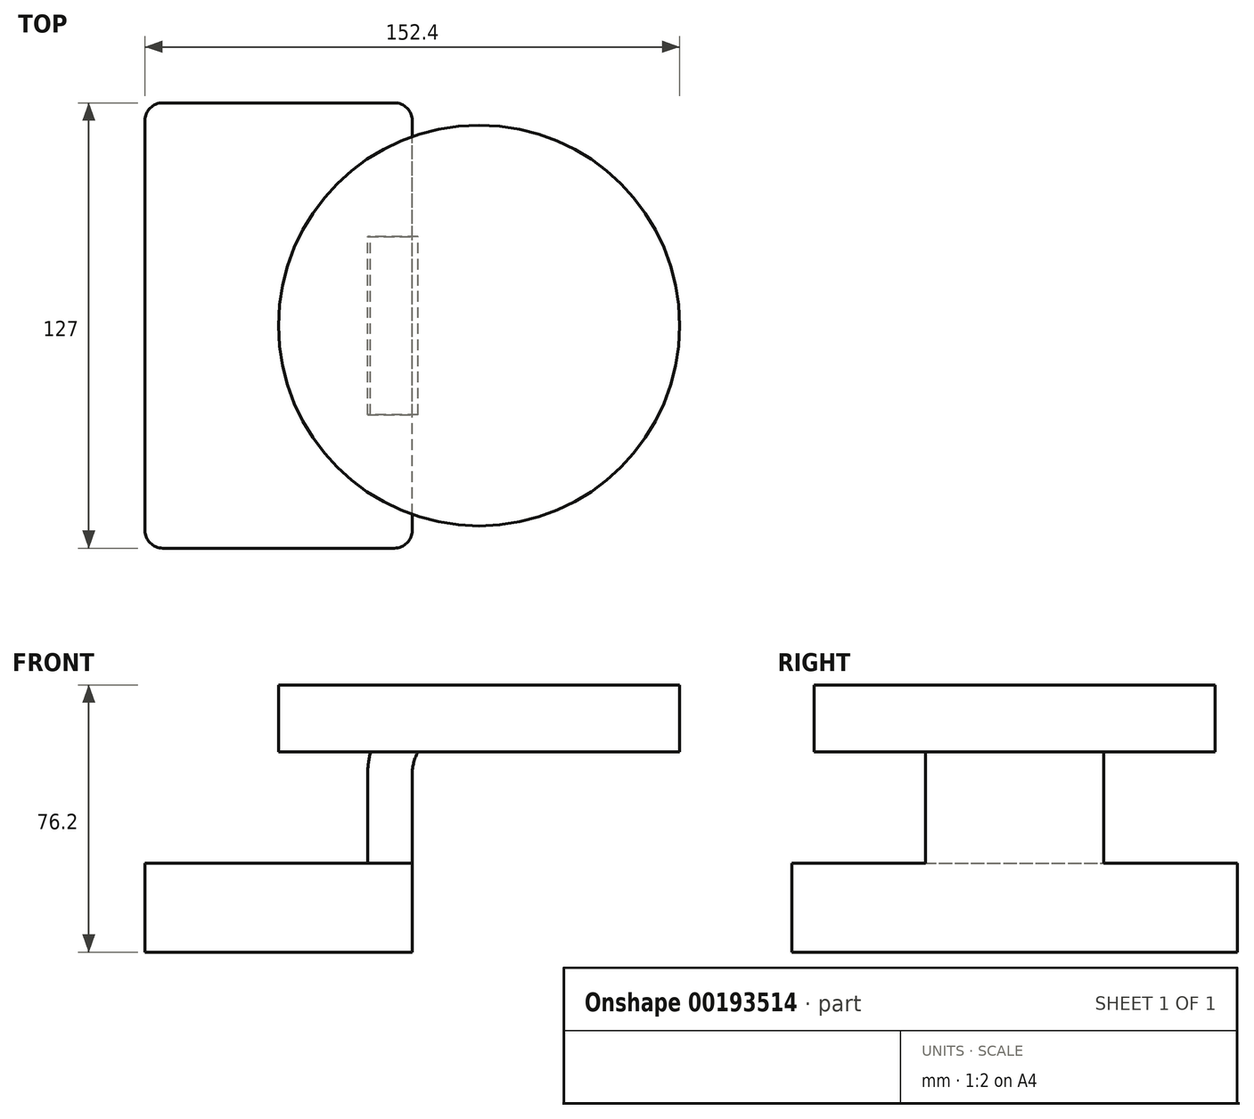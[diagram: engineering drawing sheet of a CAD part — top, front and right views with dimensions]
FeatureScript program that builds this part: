
annotation { "Feature Type Name" : "Feature", "Feature Type Description" : "" }
export const myFeature = defineFeature(function(context is Context, id is Id, definition is map)
    precondition{}
    {
        {
            var Q0;
            Q0=qCreatedBy(makeId("Front.planeOp"),FACE);
            var sketch = newSketch(context, id + "F0", { "sketchPlane" : qUnion([Q0])});
            skLineSegment(sketch, "E0.bottom", {"start": v(-38.1, -12.7) * mm, "end": v(38.1, -12.7) * mm});
            skLineSegment(sketch, "E0.top", {"start": v(-38.1, 12.7) * mm, "end": v(38.1, 12.7) * mm});
            skLineSegment(sketch, "E0.left", {"start": v(-38.1, -12.7) * mm, "end": v(-38.1, 12.7) * mm});
            skLineSegment(sketch, "E0.right", {"start": v(38.1, -12.7) * mm, "end": v(38.1, 12.7) * mm});
            skPoint(sketch, "E0.middle", {"position": v(0, 0) * mm});
            skLineSegment(sketch, "E1.bottom", {"start": v(114.3, 44.45) * mm, "end": v(57.15, 44.45) * mm});
            skLineSegment(sketch, "E1.top", {"start": v(114.3, 63.5) * mm, "end": v(57.15, 63.5) * mm});
            skLineSegment(sketch, "E1.left", {"start": v(114.3, 44.45) * mm, "end": v(114.3, 63.5) * mm});
            skLineSegment(sketch, "E1.right", {"start": v(57.15, 44.45) * mm, "end": v(57.15, 63.5) * mm});
            skPoint(sketch, "E1.middle", {"position": v(85.72, 53.98) * mm});
            skLineSegment(sketch, "E2", {"start": v(38.1, 12.7) * mm, "end": v(38.1, 38.1) * mm});
            skArc(sketch, "E3", {"start": v(38.1, 38.1) * mm, "mid": v(41.82, 47.08) * mm, "end": v(50.8, 50.8) * mm});
            skLineSegment(sketch, "E4", {"start": v(50.8, 50.8) * mm, "end": v(76.65, 50.8) * mm});
            skLineSegment(sketch, "E5.0", {"start": v(50.8, 63.5) * mm, "end": v(76.65, 63.5) * mm});
            skArc(sketch, "E5.1", {"start": v(25.4, 38.1) * mm, "mid": v(32.84, 56.06) * mm, "end": v(50.8, 63.5) * mm});
            skLineSegment(sketch, "E5.2", {"start": v(25.4, 12.7) * mm, "end": v(25.4, 38.1) * mm});
            skFitSpline(sketch, "E6", {"points": [v(-38.1, 12.7) * mm, v(50.8, 63.5) * mm], "startDerivative": vector(61.03, 117.74) * mm, "endDerivative": vector(137.3, -0.66) * mm});
            skSolve(sketch);
        }
        {
            var Q0;
            Q0=makeQuery(id+"F0.imprint","IMPRINT",FACE,{"disambiguationData":[TD([[makeQuery(id+"F0.imprint","IMPRINT",EDGE,{"derivedFrom":sQuery(id+"F0.wireOp",EDGE,"E0.bottom")}),1.0]])]});
            extrude(context, id + "F1", {"entities" : qUnion([Q0]), "endBound" : BoundingType.SYMMETRIC, "depth" : 127 * mm});
        }
        {
            var Q0;
            {var subQ1=sQuery(id+"F0.wireOp",EDGE,"E2");Q0=makeQuery(id+"F0.imprint","IMPRINT",FACE,{"disambiguationData":[TD([[makeQuery(id+"F0.imprint","IMPRINT",EDGE,{"derivedFrom":subQ1}),1.0]])]});}
            extrude(context, id + "F2", {"entities" : qUnion([Q0]), "operationType" : NewBodyOperationType.ADD, "endBound" : BoundingType.SYMMETRIC, "depth" : 50.8 * mm});
        }
        {
            var Q0;
            Q0=makeQuery(id+"F0.imprint","IMPRINT",FACE,{"disambiguationData":[TD([[makeQuery(id+"F0.imprint","IMPRINT",EDGE,{"derivedFrom":sQuery(id+"F0.wireOp",EDGE,"E5.1")}),1.0]])]});
            extrude(context, id + "F3", {"entities" : qUnion([Q0]), "operationType" : NewBodyOperationType.ADD, "endBound" : BoundingType.SYMMETRIC, "depth" : 25.4 * mm});
        }
        {
            var Q0;
            {var subQ1=sQuery(id+"F0.wireOp",EDGE,"E1.bottom");Q0=makeQuery(id+"F0.imprint","IMPRINT",FACE,{"disambiguationData":[TD([[makeQuery(id+"F0.imprint","IMPRINT",EDGE,{"derivedFrom":subQ1}),-1.0]])]});}
            var Q1;
            Q1=sQuery(id+"F0.wireOp",EDGE,"E1.right");
            revolve(context, id + "F4", {"operationType" : NewBodyOperationType.ADD, "entities" : qUnion([Q0]), "axis" : qUnion([Q1]), "revolveType" : RevolveType.FULL});
        }
        {
            var Q0;
            Q0=makeQuery(id+"F1.opExtrude","CAP_EDGE",EDGE,{"disambiguationData":[OSD([sQuery(id+"F0.wireOp",EDGE,"E0.left")])],"isStart":false});
            var Q1;
            Q1=makeQuery(id+"F1.opExtrude","CAP_EDGE",EDGE,{"disambiguationData":[OSD([sQuery(id+"F0.wireOp",EDGE,"E0.right")])],"isStart":false});
            var Q2;
            Q2=makeQuery(id+"F1.opExtrude","CAP_EDGE",EDGE,{"disambiguationData":[OSD([sQuery(id+"F0.wireOp",EDGE,"E0.left")])],"isStart":true});
            var Q3;
            Q3=makeQuery(id+"F1.opExtrude","CAP_EDGE",EDGE,{"disambiguationData":[OSD([sQuery(id+"F0.wireOp",EDGE,"E0.right")])],"isStart":true});
            fillet(context, id + "F5", {"entities" : qUnion([Q0, Q1, Q2, Q3]), "radius" : 5.08 * mm, "tangentPropagation" : true, "allowEdgeOverflow" : false});
        }
    });
